# Revit family: Zumtobel ECOOS2 SLIM
name_source: partatom
category: Lighting Fixtures
revit_build: Autodesk Revit 2016 (Build: 20150220_1215(x64)
units: mm (PartAtom-declared; Revit-internal decimal feet)

## family parameters
Cut with Voids When Loaded = No
Host = Face
Light Source = Yes
OmniClass Number = 23.80.70.11
OmniClass Title = Luminaries for Internal Lighting
Part Type = Normal
Room Calculation Point = No
Round Connector Dimension = Use Diameter
Shared = No

## types (4) — shared parameters
Assembly Code = D5020200
Body = ZG_Metal_Light_Grey
Color Filter = 16777215
Cover = ZG_PMMA_Opaque
Dimming Lamp Color Temperature Shift = <None>
Emit Shape Visible in Rendering = No
Emit from Rectangle Length = 152 mm  [stored 0.498688 ft]
Height = 48 mm  [stored 0.15748 ft]
Lamp = LED
Manufacturer = Zumtobel Lighting
Tilt Angle = -90.00°
Voltage = 230 V
Width = 152 mm  [stored 0.498688 ft]
zero-valued in all types: Default Elevation

## per-type parameters (varying)
| type | Apparent Load | Description | Emit from Rectangle Width | Length | Model | No TEC Track Mount | Photometric Web File | TEC Track Mount | URL |
| ECOOS2 SLIM 5500 L15 | 60 VA | Surface mount or pendant LED luminaire | 1499 mm  [stored 4.91798 ft] | 1512 mm  [stored 4.96063 ft] | 42932550 | Yes | 42932550_(STD_LEO).IES | No | www.zumtobel.de/42932550 |
| ECOOS2 SLIM 4400 L12 | 40 VA | Surface mount or pendant LED luminaire | 1251 mm  [stored 4.10433 ft] | 1264 mm | 42186826 | Yes | 42186826_(STD_LEO).IES | No | www.zumtobel.de/42186826 |
| ECOOS2 SLIM 5500 TEC L15 | 60 VA | TECTON track mount LED luminaire | 1499 mm  [stored 4.91798 ft] | 1512 mm  [stored 4.96063 ft] | 42932553 | No | 42932553_(STD_LEO).IES | Yes | www.zumtobel.de/42932553 |
| ECOOS2 SLIM 4400 TEC L12 | 40 VA | TECTON track mount LED luminaire | 1251 mm  [stored 4.10433 ft] | 1264 mm | 42933406 | No | 42933406_(STD_LEO).IES | Yes | www.zumtobel.de/42933406 |

note: [stored X ft] marks values corroborated as IEEE doubles in the binary element streams (Revit-internal decimal feet)

## geometry (parser evidence)
native form markers: Blend x2, Sweep x7
no freeform markers — native parametric forms only
